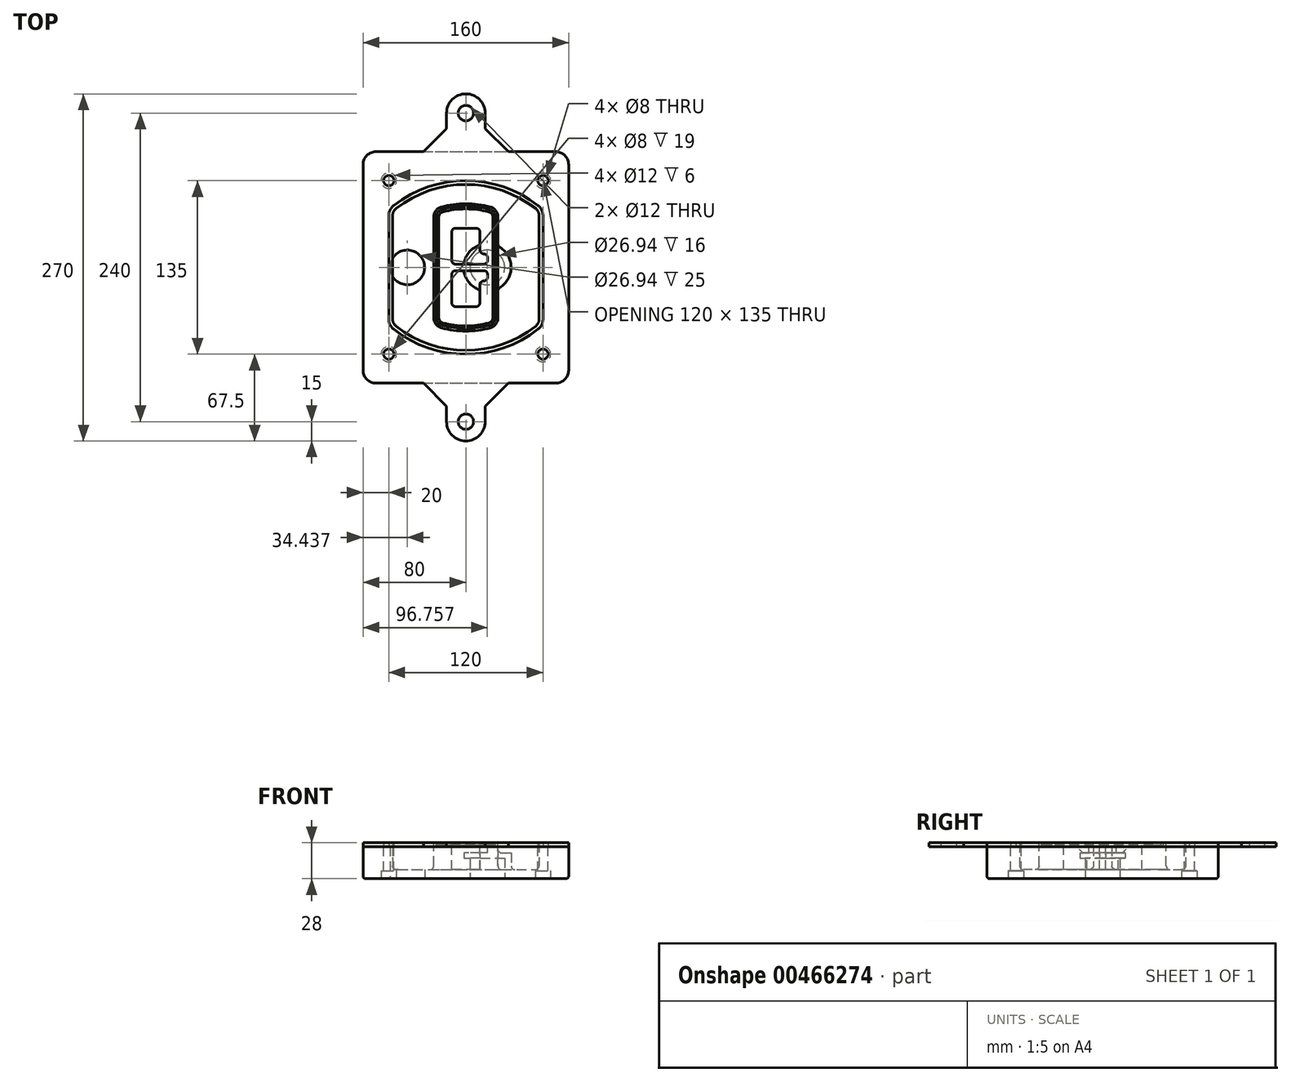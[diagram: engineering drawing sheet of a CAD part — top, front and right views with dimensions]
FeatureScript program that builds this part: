
annotation { "Feature Type Name" : "Feature", "Feature Type Description" : "" }
export const myFeature = defineFeature(function(context is Context, id is Id, definition is map)
    precondition{}
    {
        {
            var Q0;
            Q0=qCreatedBy(makeId("Top.planeOp"),FACE);
            var sketch = newSketch(context, id + "F0", { "sketchPlane" : qUnion([Q0])});
            skPoint(sketch, "E0.rect.middle", {"position": v(0, 0) * mm});
            skLineSegment(sketch, "E1.bottom", {"start": v(-70, -90) * mm, "end": v(70, -90) * mm});
            skLineSegment(sketch, "E1.top", {"start": v(-70, 90) * mm, "end": v(70, 90) * mm});
            skLineSegment(sketch, "E1.left", {"start": v(-80, -80) * mm, "end": v(-80, 80) * mm});
            skLineSegment(sketch, "E1.right", {"start": v(80, -80) * mm, "end": v(80, 80) * mm});
            skLineSegment(sketch, "E2", {"start": v(-80, 90) * mm, "end": v(80, -90) * mm, "construction": true});
            skLineSegment(sketch, "E3", {"start": v(80, 90) * mm, "end": v(-80, -90) * mm, "construction": true});
            skCircle(sketch, "E4", {"center": v(-60, 67.5) * mm, "radius": 4 * mm});
            skCircle(sketch, "E5", {"center": v(60, 67.5) * mm, "radius": 4 * mm});
            skCircle(sketch, "E6", {"center": v(60, -67.5) * mm, "radius": 4 * mm});
            skCircle(sketch, "E7", {"center": v(-60, -67.5) * mm, "radius": 4 * mm});
            skLineSegment(sketch, "E8", {"start": v(-60, 67.5) * mm, "end": v(60, 67.5) * mm, "construction": true});
            skLineSegment(sketch, "E9", {"start": v(60, 67.5) * mm, "end": v(60, -67.5) * mm, "construction": true});
            skLineSegment(sketch, "E10", {"start": v(60, -67.5) * mm, "end": v(-60, -67.5) * mm, "construction": true});
            skLineSegment(sketch, "E11", {"start": v(-60, -67.5) * mm, "end": v(-60, 67.5) * mm, "construction": true});
            skLineSegment(sketch, "E12", {"start": v(-60, 40.3) * mm, "end": v(-60, -40.3) * mm});
            skLineSegment(sketch, "E13", {"start": v(60, 40.3) * mm, "end": v(60, -40.3) * mm});
            skArc(sketch, "E14", {"start": v(56.15, 48.18) * mm, "mid": v(0, 67.5) * mm, "end": v(-56.15, 48.18) * mm});
            skArc(sketch, "E15", {"start": v(-56.15, -48.18) * mm, "mid": v(0, -67.5) * mm, "end": v(56.15, -48.18) * mm});
            skLineSegment(sketch, "E16", {"start": v(-60, 0) * mm, "end": v(60, 0) * mm, "construction": true});
            skPoint(sketch, "E17.visualSharp", {"position": v(-60, -45) * mm});
            skArc(sketch, "E17.filletArc", {"start": v(-60, -40.3) * mm, "mid": v(-58.99, -44.68) * mm, "end": v(-56.15, -48.18) * mm});
            skPoint(sketch, "E18.visualSharp", {"position": v(-60, 45) * mm});
            skArc(sketch, "E18.filletArc", {"start": v(-56.15, 48.18) * mm, "mid": v(-58.99, 44.68) * mm, "end": v(-60, 40.3) * mm});
            skPoint(sketch, "E19.visualSharp", {"position": v(60, 45) * mm});
            skArc(sketch, "E19.filletArc", {"start": v(60, 40.3) * mm, "mid": v(58.99, 44.68) * mm, "end": v(56.15, 48.18) * mm});
            skPoint(sketch, "E20.visualSharp", {"position": v(60, -45) * mm});
            skArc(sketch, "E20.filletArc", {"start": v(56.15, -48.18) * mm, "mid": v(58.99, -44.68) * mm, "end": v(60, -40.3) * mm});
            skPoint(sketch, "E21.visualSharp", {"position": v(-80, 90) * mm});
            skArc(sketch, "E21.filletArc", {"start": v(-70, 90) * mm, "mid": v(-77.07, 87.07) * mm, "end": v(-80, 80) * mm});
            skPoint(sketch, "E22.visualSharp", {"position": v(80, 90) * mm});
            skArc(sketch, "E22.filletArc", {"start": v(80, 80) * mm, "mid": v(77.07, 87.07) * mm, "end": v(70, 90) * mm});
            skPoint(sketch, "E23.visualSharp", {"position": v(80, -90) * mm});
            skArc(sketch, "E23.filletArc", {"start": v(70, -90) * mm, "mid": v(77.07, -87.07) * mm, "end": v(80, -80) * mm});
            skPoint(sketch, "E24.visualSharp", {"position": v(-80, -90) * mm});
            skArc(sketch, "E24.filletArc", {"start": v(-80, -80) * mm, "mid": v(-77.07, -87.07) * mm, "end": v(-70, -90) * mm});
            skArc(sketch, "E25.0", {"start": v(57, 40.3) * mm, "mid": v(56.3, 43.36) * mm, "end": v(54.3, 45.81) * mm});
            skLineSegment(sketch, "E25.1", {"start": v(57, 40.3) * mm, "end": v(57, -40.3) * mm});
            skArc(sketch, "E25.2", {"start": v(54.3, -45.81) * mm, "mid": v(56.3, -43.36) * mm, "end": v(57, -40.3) * mm});
            skArc(sketch, "E25.3", {"start": v(-54.3, -45.81) * mm, "mid": v(0, -64.5) * mm, "end": v(54.3, -45.81) * mm});
            skArc(sketch, "E25.4", {"start": v(-57, -40.3) * mm, "mid": v(-56.3, -43.36) * mm, "end": v(-54.3, -45.81) * mm});
            skArc(sketch, "E25.5", {"start": v(54.3, 45.81) * mm, "mid": v(0, 64.5) * mm, "end": v(-54.3, 45.81) * mm});
            skLineSegment(sketch, "E25.6", {"start": v(-57, 40.3) * mm, "end": v(-57, -40.3) * mm});
            skArc(sketch, "E25.7", {"start": v(-54.3, 45.81) * mm, "mid": v(-56.3, 43.36) * mm, "end": v(-57, 40.3) * mm});
            skArc(sketch, "E26.0", {"start": v(-58.62, 51.33) * mm, "mid": v(-62.58, 46.43) * mm, "end": v(-64, 40.3) * mm});
            skArc(sketch, "E26.1", {"start": v(58.62, 51.33) * mm, "mid": v(0, 71.5) * mm, "end": v(-58.62, 51.33) * mm});
            skArc(sketch, "E26.2", {"start": v(64, 40.3) * mm, "mid": v(62.58, 46.43) * mm, "end": v(58.62, 51.33) * mm});
            skLineSegment(sketch, "E26.3", {"start": v(64, 40.3) * mm, "end": v(64, -40.3) * mm});
            skArc(sketch, "E26.4", {"start": v(58.62, -51.33) * mm, "mid": v(62.58, -46.43) * mm, "end": v(64, -40.3) * mm});
            skLineSegment(sketch, "E26.5", {"start": v(-64, 40.3) * mm, "end": v(-64, -40.3) * mm});
            skArc(sketch, "E26.6", {"start": v(-58.62, -51.33) * mm, "mid": v(0, -71.5) * mm, "end": v(58.62, -51.33) * mm});
            skArc(sketch, "E26.7", {"start": v(-64, -40.3) * mm, "mid": v(-62.58, -46.43) * mm, "end": v(-58.62, -51.33) * mm});
            skSolve(sketch);
        }
        {
            var Q0;
            Q0=makeQuery(id+"F0.imprint","IMPRINT",FACE,{"disambiguationData":[TD([[makeQuery(id+"F0.imprint","IMPRINT",EDGE,{"derivedFrom":sQuery(id+"F0.wireOp",EDGE,"E1.bottom")}),1.0]])]});
            var Q1;
            Q1=makeQuery(id+"F0.imprint","IMPRINT",FACE,{"disambiguationData":[TD([[makeQuery(id+"F0.imprint","IMPRINT",EDGE,{"derivedFrom":sQuery(id+"F0.wireOp",EDGE,"E12")}),1.0]])]});
            var Q2;
            Q2=makeQuery(id+"F0.imprint","IMPRINT",FACE,{"disambiguationData":[TD([[makeQuery(id+"F0.imprint","IMPRINT",EDGE,{"derivedFrom":sQuery(id+"F0.wireOp",EDGE,"E25.0")}),1.0]])]});
            var Q3;
            Q3=makeQuery(id+"F0.imprint","IMPRINT",FACE,{"disambiguationData":[TD([[makeQuery(id+"F0.imprint","IMPRINT",EDGE,{"derivedFrom":sQuery(id+"F0.wireOp",EDGE,"E12")}),-1.0]])]});
            extrude(context, id + "F1", {"entities" : qUnion([Q0, Q1, Q2, Q3]), "oppositeDirection" : true, "depth" : 25 * mm});
        }
        {
            var Q0;
            Q0=makeQuery(id+"F0.imprint","IMPRINT",FACE,{"disambiguationData":[TD([[makeQuery(id+"F0.imprint","IMPRINT",EDGE,{"derivedFrom":sQuery(id+"F0.wireOp",EDGE,"E12")}),1.0]])]});
            extrude(context, id + "F2", {"entities" : qUnion([Q0]), "operationType" : NewBodyOperationType.ADD, "depth" : 3 * mm});
        }
        {
            var Q0;
            Q0=makeQuery(id+"F0.imprint","IMPRINT",FACE,{"disambiguationData":[TD([[makeQuery(id+"F0.imprint","IMPRINT",EDGE,{"derivedFrom":sQuery(id+"F0.wireOp",EDGE,"E25.0")}),1.0]])]});
            extrude(context, id + "F3", {"entities" : qUnion([Q0]), "operationType" : NewBodyOperationType.REMOVE, "oppositeDirection" : true, "depth" : 18 * mm});
        }
        {
            var Q0;
            Q0=makeQuery(id+"F2.opExtrude","CAP_FACE",FACE,{"disambiguationData":[OSD([sQuery(id+"F0.wireOp",EDGE,"E12"),sQuery(id+"F0.wireOp",EDGE,"E13"),sQuery(id+"F0.wireOp",EDGE,"E14"),sQuery(id+"F0.wireOp",EDGE,"E15"),sQuery(id+"F0.wireOp",EDGE,"E17.filletArc"),sQuery(id+"F0.wireOp",EDGE,"E18.filletArc"),sQuery(id+"F0.wireOp",EDGE,"E19.filletArc"),sQuery(id+"F0.wireOp",EDGE,"E20.filletArc"),sQuery(id+"F0.wireOp",EDGE,"E25.0"),sQuery(id+"F0.wireOp",EDGE,"E25.1"),sQuery(id+"F0.wireOp",EDGE,"E25.2"),sQuery(id+"F0.wireOp",EDGE,"E25.3"),sQuery(id+"F0.wireOp",EDGE,"E25.4"),sQuery(id+"F0.wireOp",EDGE,"E25.5"),sQuery(id+"F0.wireOp",EDGE,"E25.6"),sQuery(id+"F0.wireOp",EDGE,"E25.7")])],"isStart":false});
            var sketch = newSketch(context, id + "F4", { "sketchPlane" : qUnion([Q0])});
            skArc(sketch, "E27.0", {"start": v(-19.08, -46.97) * mm, "mid": v(0, -49.5) * mm, "end": v(19.08, -46.97) * mm});
            skArc(sketch, "E28.0", {"start": v(19.08, 46.97) * mm, "mid": v(0, 49.5) * mm, "end": v(-19.08, 46.97) * mm});
            skLineSegment(sketch, "E29", {"start": v(-25, 39.25) * mm, "end": v(-25, -39.25) * mm});
            skLineSegment(sketch, "E30", {"start": v(25, 39.25) * mm, "end": v(25, -39.25) * mm});
            skLineSegment(sketch, "E31", {"start": v(-25, 45.1) * mm, "end": v(25, 45.1) * mm, "construction": true});
            skLineSegment(sketch, "E32", {"start": v(-25, -45.1) * mm, "end": v(25, -45.1) * mm, "construction": true});
            skPoint(sketch, "E33.visualSharp", {"position": v(-25, 45.1) * mm});
            skArc(sketch, "E33.filletArc", {"start": v(-19.08, 46.97) * mm, "mid": v(-23.35, 44.11) * mm, "end": v(-25, 39.25) * mm});
            skPoint(sketch, "E34.visualSharp", {"position": v(25, 45.1) * mm});
            skArc(sketch, "E34.filletArc", {"start": v(25, 39.25) * mm, "mid": v(23.35, 44.11) * mm, "end": v(19.08, 46.97) * mm});
            skPoint(sketch, "E35.visualSharp", {"position": v(25, -45.1) * mm});
            skArc(sketch, "E35.filletArc", {"start": v(19.08, -46.97) * mm, "mid": v(23.35, -44.11) * mm, "end": v(25, -39.25) * mm});
            skPoint(sketch, "E36.visualSharp", {"position": v(-25, -45.1) * mm});
            skArc(sketch, "E36.filletArc", {"start": v(-25, -39.25) * mm, "mid": v(-23.35, -44.11) * mm, "end": v(-19.08, -46.97) * mm});
            skArc(sketch, "E37.0", {"start": v(54.3, 45.81) * mm, "mid": v(0, 64.5) * mm, "end": v(-54.3, 45.81) * mm});
            skArc(sketch, "E37.1", {"start": v(-54.3, 45.81) * mm, "mid": v(-56.3, 43.36) * mm, "end": v(-57, 40.3) * mm});
            skLineSegment(sketch, "E37.2", {"start": v(-57, 40.3) * mm, "end": v(-57, -40.3) * mm});
            skArc(sketch, "E37.3", {"start": v(-57, -40.3) * mm, "mid": v(-56.3, -43.36) * mm, "end": v(-54.3, -45.81) * mm});
            skArc(sketch, "E37.4", {"start": v(-54.3, -45.81) * mm, "mid": v(0, -64.5) * mm, "end": v(54.3, -45.81) * mm});
            skArc(sketch, "E37.5", {"start": v(54.3, -45.81) * mm, "mid": v(56.3, -43.36) * mm, "end": v(57, -40.3) * mm});
            skLineSegment(sketch, "E37.6", {"start": v(57, 40.3) * mm, "end": v(57, -40.3) * mm});
            skArc(sketch, "E37.7", {"start": v(57, 40.3) * mm, "mid": v(56.3, 43.36) * mm, "end": v(54.3, 45.81) * mm});
            skLineSegment(sketch, "E38.0", {"start": v(23, 39.25) * mm, "end": v(23, -39.25) * mm});
            skArc(sketch, "E38.1", {"start": v(18.56, -45.04) * mm, "mid": v(21.76, -42.9) * mm, "end": v(23, -39.25) * mm});
            skArc(sketch, "E38.2", {"start": v(-18.56, -45.04) * mm, "mid": v(0, -47.5) * mm, "end": v(18.56, -45.04) * mm});
            skArc(sketch, "E38.3", {"start": v(-23, -39.25) * mm, "mid": v(-21.76, -42.9) * mm, "end": v(-18.56, -45.04) * mm});
            skLineSegment(sketch, "E38.4", {"start": v(-23, 39.25) * mm, "end": v(-23, -39.25) * mm});
            skArc(sketch, "E38.5", {"start": v(23, 39.25) * mm, "mid": v(21.76, 42.9) * mm, "end": v(18.56, 45.04) * mm});
            skArc(sketch, "E38.6", {"start": v(-18.56, 45.04) * mm, "mid": v(-21.76, 42.9) * mm, "end": v(-23, 39.25) * mm});
            skArc(sketch, "E38.7", {"start": v(18.56, 45.04) * mm, "mid": v(0, 47.5) * mm, "end": v(-18.56, 45.04) * mm});
            skArc(sketch, "E39.0", {"start": v(21, 39.25) * mm, "mid": v(20.18, 41.68) * mm, "end": v(18.04, 43.1) * mm});
            skLineSegment(sketch, "E39.1", {"start": v(21, 39.25) * mm, "end": v(21, -39.25) * mm});
            skArc(sketch, "E39.2", {"start": v(18.04, -43.1) * mm, "mid": v(20.18, -41.68) * mm, "end": v(21, -39.25) * mm});
            skArc(sketch, "E39.3", {"start": v(-18.04, -43.1) * mm, "mid": v(0, -45.5) * mm, "end": v(18.04, -43.1) * mm});
            skArc(sketch, "E39.4", {"start": v(-21, -39.25) * mm, "mid": v(-20.18, -41.68) * mm, "end": v(-18.04, -43.1) * mm});
            skArc(sketch, "E39.5", {"start": v(18.04, 43.1) * mm, "mid": v(0, 45.5) * mm, "end": v(-18.04, 43.1) * mm});
            skLineSegment(sketch, "E39.6", {"start": v(-21, 39.25) * mm, "end": v(-21, -39.25) * mm});
            skArc(sketch, "E39.7", {"start": v(-18.04, 43.1) * mm, "mid": v(-20.18, 41.68) * mm, "end": v(-21, 39.25) * mm});
            skLineSegment(sketch, "E40", {"start": v(-25, 0) * mm, "end": v(25, 0) * mm, "construction": true});
            skLineSegment(sketch, "E41", {"start": v(-11, 5.5) * mm, "end": v(-11, 27.5) * mm});
            skLineSegment(sketch, "E42", {"start": v(-8, 30.5) * mm, "end": v(8, 30.5) * mm});
            skLineSegment(sketch, "E43", {"start": v(11, 27.5) * mm, "end": v(11, 13.5) * mm});
            skLineSegment(sketch, "E44", {"start": v(14, 10.5) * mm, "end": v(14, 10.5) * mm});
            skLineSegment(sketch, "E45", {"start": v(17, 7.5) * mm, "end": v(17, 5.5) * mm});
            skLineSegment(sketch, "E46", {"start": v(14, 2.5) * mm, "end": v(-8, 2.5) * mm});
            skPoint(sketch, "E47.visualSharp", {"position": v(-11, 30.5) * mm});
            skArc(sketch, "E47.filletArc", {"start": v(-8, 30.5) * mm, "mid": v(-10.12, 29.62) * mm, "end": v(-11, 27.5) * mm});
            skPoint(sketch, "E48.visualSharp", {"position": v(11, 30.5) * mm});
            skArc(sketch, "E48.filletArc", {"start": v(11, 27.5) * mm, "mid": v(10.12, 29.62) * mm, "end": v(8, 30.5) * mm});
            skPoint(sketch, "E49.visualSharp", {"position": v(11, 10.5) * mm});
            skArc(sketch, "E49.filletArc", {"start": v(11, 13.5) * mm, "mid": v(11.88, 11.38) * mm, "end": v(14, 10.5) * mm});
            skPoint(sketch, "E50.visualSharp", {"position": v(17, 10.5) * mm});
            skArc(sketch, "E50.filletArc", {"start": v(17, 7.5) * mm, "mid": v(16.12, 9.62) * mm, "end": v(14, 10.5) * mm});
            skPoint(sketch, "E51.visualSharp", {"position": v(17, 2.5) * mm});
            skArc(sketch, "E51.filletArc", {"start": v(14, 2.5) * mm, "mid": v(16.12, 3.38) * mm, "end": v(17, 5.5) * mm});
            skPoint(sketch, "E52.visualSharp", {"position": v(-11, 2.5) * mm});
            skArc(sketch, "E52.filletArc", {"start": v(-11, 5.5) * mm, "mid": v(-10.12, 3.38) * mm, "end": v(-8, 2.5) * mm});
            skLineSegment(sketch, "E53.0.MirrorCS", {"start": v(14, -2.5) * mm, "end": v(-8, -2.5) * mm});
            skArc(sketch, "E54.0.MirrorCS", {"start": v(-11, -5.5) * mm, "mid": v(-10.12, -3.38) * mm, "end": v(-8, -2.5) * mm});
            skLineSegment(sketch, "E55.0.MirrorCS", {"start": v(-11, -5.5) * mm, "end": v(-11, -27.5) * mm});
            skArc(sketch, "E56.0.MirrorCS", {"start": v(-8, -30.5) * mm, "mid": v(-10.12, -29.62) * mm, "end": v(-11, -27.5) * mm});
            skLineSegment(sketch, "E57.0.MirrorCS", {"start": v(-8, -30.5) * mm, "end": v(8, -30.5) * mm});
            skArc(sketch, "E58.0.MirrorCS", {"start": v(11, -27.5) * mm, "mid": v(10.12, -29.62) * mm, "end": v(8, -30.5) * mm});
            skLineSegment(sketch, "E59.0.MirrorCS", {"start": v(11, -27.5) * mm, "end": v(11, -13.5) * mm});
            skArc(sketch, "E60.0.MirrorCS", {"start": v(11, -13.5) * mm, "mid": v(11.88, -11.38) * mm, "end": v(14, -10.5) * mm});
            skArc(sketch, "E61.0.MirrorCS", {"start": v(17, -7.5) * mm, "mid": v(16.12, -9.62) * mm, "end": v(14, -10.5) * mm});
            skLineSegment(sketch, "E62.0.MirrorCS", {"start": v(17, -7.5) * mm, "end": v(17, -5.5) * mm});
            skArc(sketch, "E63.0.MirrorCS", {"start": v(14, -2.5) * mm, "mid": v(16.12, -3.38) * mm, "end": v(17, -5.5) * mm});
            skSolve(sketch);
        }
        {
            var Q0;
            Q0=makeQuery(id+"F4.imprint","IMPRINT",FACE,{"disambiguationData":[TD([[makeQuery(id+"F4.imprint","IMPRINT",EDGE,{"derivedFrom":sQuery(id+"F4.wireOp",EDGE,"E27.0")}),1.0]])]});
            var Q1;
            Q1=makeQuery(id+"F4.imprint","IMPRINT",FACE,{"disambiguationData":[TD([[makeQuery(id+"F4.imprint","IMPRINT",EDGE,{"derivedFrom":sQuery(id+"F4.wireOp",EDGE,"E38.0")}),-1.0]])]});
            var Q2;
            Q2=makeQuery(id+"F4.imprint","IMPRINT",FACE,{"disambiguationData":[TD([[makeQuery(id+"F4.imprint","IMPRINT",EDGE,{"derivedFrom":sQuery(id+"F4.wireOp",EDGE,"E39.0")}),1.0]])]});
            extrude(context, id + "F5", {"entities" : qUnion([Q0, Q1, Q2]), "operationType" : NewBodyOperationType.ADD, "endBound" : BoundingType.UP_TO_NEXT, "oppositeDirection" : true, "depth" : 25 * mm});
        }
        {
            var Q0;
            Q0=makeQuery(id+"F4.imprint","IMPRINT",FACE,{"disambiguationData":[TD([[makeQuery(id+"F4.imprint","IMPRINT",EDGE,{"derivedFrom":sQuery(id+"F4.wireOp",EDGE,"E38.0")}),-1.0]])]});
            extrude(context, id + "F6", {"entities" : qUnion([Q0]), "operationType" : NewBodyOperationType.REMOVE, "oppositeDirection" : true, "depth" : 2 * mm});
        }
        {
            var Q0;
            Q0=makeQuery(id+"F1.opExtrude","CAP_FACE",FACE,{"disambiguationData":[OSD([sQuery(id+"F0.wireOp",EDGE,"E1.bottom"),sQuery(id+"F0.wireOp",EDGE,"E1.top"),sQuery(id+"F0.wireOp",EDGE,"E1.left"),sQuery(id+"F0.wireOp",EDGE,"E1.right"),sQuery(id+"F0.wireOp",EDGE,"E4"),sQuery(id+"F0.wireOp",EDGE,"E5"),sQuery(id+"F0.wireOp",EDGE,"E6"),sQuery(id+"F0.wireOp",EDGE,"E7"),sQuery(id+"F0.wireOp",EDGE,"E21.filletArc"),sQuery(id+"F0.wireOp",EDGE,"E22.filletArc"),sQuery(id+"F0.wireOp",EDGE,"E23.filletArc"),sQuery(id+"F0.wireOp",EDGE,"E24.filletArc")])],"isStart":false});
            var sketch = newSketch(context, id + "F7", { "sketchPlane" : qUnion([Q0])});
            skCircle(sketch, "E64", {"center": v(16.76, 0) * mm, "radius": 13.47 * mm});
            skCircle(sketch, "E65", {"center": v(-45.56, 0) * mm, "radius": 13.47 * mm});
            skLineSegment(sketch, "E66", {"start": v(80, 0) * mm, "end": v(-80, 0) * mm});
            skCircle(sketch, "E67", {"center": v(16.76, 0) * mm, "radius": 18.47 * mm});
            skCircle(sketch, "E68", {"center": v(60, -67.5) * mm, "radius": 6 * mm});
            skCircle(sketch, "E69", {"center": v(-60, -67.5) * mm, "radius": 6 * mm});
            skCircle(sketch, "E70", {"center": v(-60, 67.5) * mm, "radius": 6 * mm});
            skCircle(sketch, "E71", {"center": v(60, 67.5) * mm, "radius": 6 * mm});
            skSolve(sketch);
        }
        {
            var Q0;
            {var subQ1=sQuery(id+"F7.wireOp",EDGE,"E66");var subQ4=sQuery(id+"F7.wireOp",EDGE,"E64");var subQ6=makeQuery(id+"F7.imprint","INTERSECT",VERTEX,{"disambiguationData":[OD(0.0)],"derivedFrom":[subQ4,subQ1]});Q0=makeQuery(id+"F7.imprint","IMPRINT",FACE,{"disambiguationData":[TD([[makeQuery(id+"F7.imprint","IMPRINT",EDGE,{"disambiguationData":[TD([[subQ6,-1.0]])],"derivedFrom":subQ4}),-1.0]])]});}
            var Q1;
            {var subQ0=sQuery(id+"F7.wireOp",EDGE,"E66");var subQ1=sQuery(id+"F7.wireOp",EDGE,"E64");var subQ3=makeQuery(id+"F7.imprint","INTERSECT",VERTEX,{"disambiguationData":[OD(0.0)],"derivedFrom":[subQ1,subQ0]});Q1=makeQuery(id+"F7.imprint","IMPRINT",FACE,{"disambiguationData":[TD([[makeQuery(id+"F7.imprint","IMPRINT",EDGE,{"disambiguationData":[TD([[subQ3,-1.0]])],"derivedFrom":subQ1}),1.0]])]});}
            var Q2;
            {var subQ0=sQuery(id+"F7.wireOp",EDGE,"E66");var subQ1=sQuery(id+"F7.wireOp",EDGE,"E64");var subQ3=makeQuery(id+"F7.imprint","INTERSECT",VERTEX,{"disambiguationData":[OD(0.0)],"derivedFrom":[subQ1,subQ0]});Q2=makeQuery(id+"F7.imprint","IMPRINT",FACE,{"disambiguationData":[TD([[makeQuery(id+"F7.imprint","IMPRINT",EDGE,{"disambiguationData":[TD([[subQ3,1.0]])],"derivedFrom":subQ1}),1.0]])]});}
            var Q3;
            {var subQ1=sQuery(id+"F7.wireOp",EDGE,"E66");var subQ4=sQuery(id+"F7.wireOp",EDGE,"E64");var subQ6=makeQuery(id+"F7.imprint","INTERSECT",VERTEX,{"disambiguationData":[OD(0.0)],"derivedFrom":[subQ4,subQ1]});Q3=makeQuery(id+"F7.imprint","IMPRINT",FACE,{"disambiguationData":[TD([[makeQuery(id+"F7.imprint","IMPRINT",EDGE,{"disambiguationData":[TD([[subQ6,1.0]])],"derivedFrom":subQ4}),-1.0]])]});}
            extrude(context, id + "F8", {"entities" : qUnion([Q0, Q1, Q2, Q3]), "operationType" : NewBodyOperationType.ADD, "oppositeDirection" : true, "depth" : 20 * mm});
        }
        {
            var Q0;
            {var subQ0=sQuery(id+"F7.wireOp",EDGE,"E66");var subQ1=sQuery(id+"F7.wireOp",EDGE,"E64");var subQ3=makeQuery(id+"F7.imprint","INTERSECT",VERTEX,{"disambiguationData":[OD(0.0)],"derivedFrom":[subQ1,subQ0]});Q0=makeQuery(id+"F7.imprint","IMPRINT",FACE,{"disambiguationData":[TD([[makeQuery(id+"F7.imprint","IMPRINT",EDGE,{"disambiguationData":[TD([[subQ3,-1.0]])],"derivedFrom":subQ1}),1.0]])]});}
            var Q1;
            {var subQ0=sQuery(id+"F7.wireOp",EDGE,"E66");var subQ1=sQuery(id+"F7.wireOp",EDGE,"E64");var subQ3=makeQuery(id+"F7.imprint","INTERSECT",VERTEX,{"disambiguationData":[OD(0.0)],"derivedFrom":[subQ1,subQ0]});Q1=makeQuery(id+"F7.imprint","IMPRINT",FACE,{"disambiguationData":[TD([[makeQuery(id+"F7.imprint","IMPRINT",EDGE,{"disambiguationData":[TD([[subQ3,1.0]])],"derivedFrom":subQ1}),1.0]])]});}
            extrude(context, id + "F9", {"entities" : qUnion([Q0, Q1]), "operationType" : NewBodyOperationType.REMOVE, "oppositeDirection" : true, "depth" : 16 * mm});
        }
        {
            var Q0;
            {var subQ0=sQuery(id+"F7.wireOp",EDGE,"E66");var subQ1=sQuery(id+"F7.wireOp",EDGE,"E65");var subQ3=makeQuery(id+"F7.imprint","INTERSECT",VERTEX,{"disambiguationData":[OD(0.0)],"derivedFrom":[subQ1,subQ0]});Q0=makeQuery(id+"F7.imprint","IMPRINT",FACE,{"disambiguationData":[TD([[makeQuery(id+"F7.imprint","IMPRINT",EDGE,{"disambiguationData":[TD([[subQ3,-1.0]])],"derivedFrom":subQ1}),1.0]])]});}
            var Q1;
            {var subQ0=sQuery(id+"F7.wireOp",EDGE,"E66");var subQ1=sQuery(id+"F7.wireOp",EDGE,"E65");var subQ3=makeQuery(id+"F7.imprint","INTERSECT",VERTEX,{"disambiguationData":[OD(0.0)],"derivedFrom":[subQ1,subQ0]});Q1=makeQuery(id+"F7.imprint","IMPRINT",FACE,{"disambiguationData":[TD([[makeQuery(id+"F7.imprint","IMPRINT",EDGE,{"disambiguationData":[TD([[subQ3,1.0]])],"derivedFrom":subQ1}),1.0]])]});}
            extrude(context, id + "F10", {"entities" : qUnion([Q0, Q1]), "operationType" : NewBodyOperationType.REMOVE, "oppositeDirection" : true, "depth" : 25 * mm});
        }
        {
            var Q0;
            Q0=makeQuery(id+"F7.imprint","IMPRINT",FACE,{"disambiguationData":[TD([[makeQuery(id+"F7.imprint","IMPRINT",EDGE,{"derivedFrom":sQuery(id+"F7.wireOp",EDGE,"E68")}),1.0]])]});
            var Q1;
            Q1=makeQuery(id+"F7.imprint","IMPRINT",FACE,{"disambiguationData":[TD([[makeQuery(id+"F7.imprint","IMPRINT",EDGE,{"derivedFrom":makeQuery(id+"F1.opExtrude","CAP_EDGE",EDGE,{"disambiguationData":[OSD([sQuery(id+"F0.wireOp",EDGE,"E5")])],"isStart":false})}),-1.0]])]});
            var Q2;
            Q2=makeQuery(id+"F7.imprint","IMPRINT",FACE,{"disambiguationData":[TD([[makeQuery(id+"F7.imprint","IMPRINT",EDGE,{"derivedFrom":sQuery(id+"F7.wireOp",EDGE,"E69")}),1.0]])]});
            var Q3;
            Q3=makeQuery(id+"F7.imprint","IMPRINT",FACE,{"disambiguationData":[TD([[makeQuery(id+"F7.imprint","IMPRINT",EDGE,{"derivedFrom":makeQuery(id+"F1.opExtrude","CAP_EDGE",EDGE,{"disambiguationData":[OSD([sQuery(id+"F0.wireOp",EDGE,"E4")])],"isStart":false})}),-1.0]])]});
            var Q4;
            Q4=makeQuery(id+"F7.imprint","IMPRINT",FACE,{"disambiguationData":[TD([[makeQuery(id+"F7.imprint","IMPRINT",EDGE,{"derivedFrom":sQuery(id+"F7.wireOp",EDGE,"E70")}),1.0]])]});
            var Q5;
            Q5=makeQuery(id+"F7.imprint","IMPRINT",FACE,{"disambiguationData":[TD([[makeQuery(id+"F7.imprint","IMPRINT",EDGE,{"derivedFrom":makeQuery(id+"F1.opExtrude","CAP_EDGE",EDGE,{"disambiguationData":[OSD([sQuery(id+"F0.wireOp",EDGE,"E7")])],"isStart":false})}),-1.0]])]});
            var Q6;
            Q6=makeQuery(id+"F7.imprint","IMPRINT",FACE,{"disambiguationData":[TD([[makeQuery(id+"F7.imprint","IMPRINT",EDGE,{"derivedFrom":sQuery(id+"F7.wireOp",EDGE,"E71")}),1.0]])]});
            var Q7;
            Q7=makeQuery(id+"F7.imprint","IMPRINT",FACE,{"disambiguationData":[TD([[makeQuery(id+"F7.imprint","IMPRINT",EDGE,{"derivedFrom":makeQuery(id+"F1.opExtrude","CAP_EDGE",EDGE,{"disambiguationData":[OSD([sQuery(id+"F0.wireOp",EDGE,"E6")])],"isStart":false})}),-1.0]])]});
            extrude(context, id + "F11", {"entities" : qUnion([Q0, Q1, Q2, Q3, Q4, Q5, Q6, Q7]), "operationType" : NewBodyOperationType.REMOVE, "oppositeDirection" : true, "depth" : 6 * mm});
        }
        {
            var Q0;
            Q0=makeQuery(id+"F9.boolean.opBoolean","COPY",FACE,{"derivedFrom":makeQuery(id+"F9.opExtrude","CAP_FACE",FACE,{"disambiguationData":[OSD([sQuery(id+"F7.wireOp",EDGE,"E64")])],"isStart":false})});
            var sketch = newSketch(context, id + "F12", { "sketchPlane" : qUnion([Q0])});
            skArc(sketch, "E72.0", {"start": v(11, 17.55) * mm, "mid": v(2.57, 11.82) * mm, "end": v(-1.54, 2.5) * mm});
            skArc(sketch, "E72.1", {"start": v(-1.54, -2.5) * mm, "mid": v(2.57, -11.82) * mm, "end": v(11, -17.55) * mm});
            skLineSegment(sketch, "E73", {"start": v(-1.54, -2.5) * mm, "end": v(14, -2.5) * mm});
            skLineSegment(sketch, "E74.0", {"start": v(14, 2.5) * mm, "end": v(-1.54, 2.5) * mm});
            skArc(sketch, "E74.1", {"start": v(14, 2.5) * mm, "mid": v(16.12, 3.38) * mm, "end": v(17, 5.5) * mm});
            skLineSegment(sketch, "E74.2", {"start": v(17, 7.5) * mm, "end": v(17, 5.5) * mm});
            skArc(sketch, "E74.3", {"start": v(17, 7.5) * mm, "mid": v(16.12, 9.62) * mm, "end": v(14, 10.5) * mm});
            skArc(sketch, "E74.4", {"start": v(11, 13.5) * mm, "mid": v(11.88, 11.38) * mm, "end": v(14, 10.5) * mm});
            skLineSegment(sketch, "E74.5", {"start": v(11, 17.55) * mm, "end": v(11, 13.5) * mm});
            skLineSegment(sketch, "E74.7", {"start": v(14, -2.5) * mm, "end": v(-1.54, -2.5) * mm});
            skArc(sketch, "E74.8", {"start": v(14, -2.5) * mm, "mid": v(16.12, -3.38) * mm, "end": v(17, -5.5) * mm});
            skLineSegment(sketch, "E74.9", {"start": v(17, -7.5) * mm, "end": v(17, -5.5) * mm});
            skArc(sketch, "E74.10", {"start": v(17, -7.5) * mm, "mid": v(16.12, -9.62) * mm, "end": v(14, -10.5) * mm});
            skArc(sketch, "E74.11", {"start": v(11, -13.5) * mm, "mid": v(11.88, -11.38) * mm, "end": v(14, -10.5) * mm});
            skLineSegment(sketch, "E74.12", {"start": v(11, -17.55) * mm, "end": v(11, -13.5) * mm});
            skPoint(sketch, "E75.orphan", {"position": v(11, -27.5) * mm});
            skPoint(sketch, "E76.orphan", {"position": v(-8, -2.5) * mm});
            skPoint(sketch, "E77.orphan", {"position": v(-8, 2.5) * mm});
            skPoint(sketch, "E78.orphan", {"position": v(11, 27.5) * mm});
            skSolve(sketch);
        }
        {
            var Q0;
            {var subQ7=sQuery(id+"F12.wireOp",EDGE,"E72.0");var subQ14=sQuery(id+"F12.wireOp",EDGE,"E72.1");var subQ16=sQuery(id+"F12.wireOp",EDGE,"E74.1");var subQ18=sQuery(id+"F12.wireOp",EDGE,"E74.8");Q0=qUnion([makeQuery(id+"F12.imprint","IMPRINT",FACE,{"disambiguationData":[TD([[makeQuery(id+"F12.imprint","IMPRINT",EDGE,{"derivedFrom":subQ7}),1.0]])]}),makeQuery(id+"F12.imprint","IMPRINT",FACE,{"disambiguationData":[TD([[makeQuery(id+"F12.imprint","IMPRINT",EDGE,{"derivedFrom":subQ14}),1.0]])]}),makeQuery(id+"F12.imprint","IMPRINT",FACE,{"disambiguationData":[TD([[makeQuery(id+"F12.imprint","IMPRINT",EDGE,{"derivedFrom":subQ16}),1.0]])]}),makeQuery(id+"F12.imprint","IMPRINT",FACE,{"disambiguationData":[TD([[makeQuery(id+"F12.imprint","IMPRINT",EDGE,{"derivedFrom":subQ18}),-1.0]])]})]);}
            var Q1;
            Q1=makeQuery(id+"F5.boolean.opBoolean","SPLIT",FACE,{"disambiguationData":[TD([makeQuery(id+"F5.opExtrude","SWEPT_FACE",FACE,{"disambiguationData":[OSD([sQuery(id+"F4.wireOp",EDGE,"E41")])]})])],"derivedFrom":makeQuery(id+"F3.boolean.opBoolean","COPY",FACE,{"derivedFrom":makeQuery(id+"F3.opExtrude","CAP_FACE",FACE,{"disambiguationData":[OSD([sQuery(id+"F0.wireOp",EDGE,"E25.0"),sQuery(id+"F0.wireOp",EDGE,"E25.1"),sQuery(id+"F0.wireOp",EDGE,"E25.2"),sQuery(id+"F0.wireOp",EDGE,"E25.3"),sQuery(id+"F0.wireOp",EDGE,"E25.4"),sQuery(id+"F0.wireOp",EDGE,"E25.5"),sQuery(id+"F0.wireOp",EDGE,"E25.6"),sQuery(id+"F0.wireOp",EDGE,"E25.7")])],"isStart":false})})});
            extrude(context, id + "F13", {"entities" : qUnion([Q0]), "operationType" : NewBodyOperationType.REMOVE, "endBound" : BoundingType.UP_TO_SURFACE, "endBoundEntityFace" : qUnion([Q1]), "depth" : 25 * mm});
        }
        {
            var Q0;
            Q0=makeQuery(id+"F3.boolean.opBoolean","COPY",EDGE,{"derivedFrom":makeQuery(id+"F3.opExtrude","CAP_EDGE",EDGE,{"disambiguationData":[OSD([sQuery(id+"F0.wireOp",EDGE,"E25.6")])],"isStart":false})});
            var Q1;
            Q1=makeQuery(id+"F8.boolean.opBoolean","INTERSECT",EDGE,{"derivedFrom":[makeQuery(id+"F5.opExtrude","SWEPT_FACE",FACE,{"disambiguationData":[OSD([sQuery(id+"F4.wireOp",EDGE,"E30")])]}),makeQuery(id+"F8.opExtrude","CAP_FACE",FACE,{"disambiguationData":[OSD([sQuery(id+"F7.wireOp",EDGE,"E67")])],"isStart":false})]});
            var Q2;
            Q2=makeQuery(id+"F8.boolean.opBoolean","INTERSECT",EDGE,{"disambiguationData":[OD(1.0)],"derivedFrom":[makeQuery(id+"F5.opExtrude","SWEPT_FACE",FACE,{"disambiguationData":[OSD([sQuery(id+"F4.wireOp",EDGE,"E30")])]}),makeQuery(id+"F8.opExtrude","SWEPT_FACE",FACE,{"disambiguationData":[OSD([sQuery(id+"F7.wireOp",EDGE,"E67")])]})]});
            var Q3;
            {var subQ0=sQuery(id+"F4.wireOp",EDGE,"E30");Q3=makeQuery(id+"F8.boolean.opBoolean","SPLIT",EDGE,{"disambiguationData":[TD([makeQuery(id+"F5.opExtrude","SWEPT_FACE",FACE,{"disambiguationData":[OSD([sQuery(id+"F4.wireOp",EDGE,"E35.filletArc")])]})])],"derivedFrom":makeQuery(id+"F5.opExtrude","CAP_EDGE",EDGE,{"disambiguationData":[OSD([subQ0])],"isStart":false})});}
            var Q4;
            {var subQ0=sQuery(id+"F0.wireOp",EDGE,"E25.7");var subQ1=sQuery(id+"F0.wireOp",EDGE,"E25.1");var subQ2=sQuery(id+"F0.wireOp",EDGE,"E25.6");var subQ3=sQuery(id+"F0.wireOp",EDGE,"E25.5");var subQ4=sQuery(id+"F0.wireOp",EDGE,"E25.4");var subQ5=sQuery(id+"F0.wireOp",EDGE,"E25.0");var subQ6=sQuery(id+"F0.wireOp",EDGE,"E25.2");var subQ7=sQuery(id+"F0.wireOp",EDGE,"E25.3");Q4=makeQuery(id+"F8.boolean.opBoolean","INTERSECT",EDGE,{"derivedFrom":[makeQuery(id+"F5.boolean.opBoolean","SPLIT",FACE,{"disambiguationData":[TD([makeQuery(id+"F2.opExtrude","SWEPT_FACE",FACE,{"disambiguationData":[OSD([subQ5])]})])],"derivedFrom":makeQuery(id+"F3.boolean.opBoolean","COPY",FACE,{"derivedFrom":makeQuery(id+"F3.opExtrude","CAP_FACE",FACE,{"disambiguationData":[OSD([subQ5,subQ1,subQ6,subQ7,subQ4,subQ3,subQ2,subQ0])],"isStart":false})})}),makeQuery(id+"F8.opExtrude","SWEPT_FACE",FACE,{"disambiguationData":[OSD([sQuery(id+"F7.wireOp",EDGE,"E67")])]})]});}
            var Q5;
            Q5=makeQuery(id+"F8.boolean.opBoolean","INTERSECT",EDGE,{"disambiguationData":[OD(0.0)],"derivedFrom":[makeQuery(id+"F5.opExtrude","SWEPT_FACE",FACE,{"disambiguationData":[OSD([sQuery(id+"F4.wireOp",EDGE,"E30")])]}),makeQuery(id+"F8.opExtrude","SWEPT_FACE",FACE,{"disambiguationData":[OSD([sQuery(id+"F7.wireOp",EDGE,"E67")])]})]});
            fillet(context, id + "F14", {"entities" : qUnion([Q0, Q1, Q2, Q3, Q4, Q5]), "radius" : 3 * mm, "tangentPropagation" : true, "allowEdgeOverflow" : false});
        }
        {
            var Q0;
            Q0=makeQuery(id+"F1.opExtrude","CAP_EDGE",EDGE,{"disambiguationData":[OSD([sQuery(id+"F0.wireOp",EDGE,"E1.bottom")])],"isStart":false});
            fillet(context, id + "F15", {"entities" : qUnion([Q0]), "radius" : 2 * mm, "tangentPropagation" : true, "allowEdgeOverflow" : false});
        }
        {
            var Q0;
            {var subQ0=sQuery(id+"F0.wireOp",EDGE,"E21.filletArc");var subQ1=sQuery(id+"F0.wireOp",EDGE,"E7");var subQ2=sQuery(id+"F0.wireOp",EDGE,"E6");var subQ3=sQuery(id+"F0.wireOp",EDGE,"E5");var subQ4=sQuery(id+"F0.wireOp",EDGE,"E4");var subQ5=sQuery(id+"F0.wireOp",EDGE,"E22.filletArc");var subQ6=sQuery(id+"F0.wireOp",EDGE,"E1.bottom");var subQ7=sQuery(id+"F0.wireOp",EDGE,"E1.right");var subQ8=sQuery(id+"F0.wireOp",EDGE,"E1.top");var subQ9=sQuery(id+"F0.wireOp",EDGE,"E1.left");var subQ10=sQuery(id+"F0.wireOp",EDGE,"E23.filletArc");var subQ11=sQuery(id+"F0.wireOp",EDGE,"E24.filletArc");Q0=makeQuery(id+"F2.boolean.opBoolean","SPLIT",FACE,{"disambiguationData":[TD([makeQuery(id+"F1.opExtrude","SWEPT_FACE",FACE,{"disambiguationData":[OSD([subQ6])]})])],"derivedFrom":makeQuery(id+"F1.opExtrude","CAP_FACE",FACE,{"disambiguationData":[OSD([subQ6,subQ8,subQ9,subQ7,subQ4,subQ3,subQ2,subQ1,subQ0,subQ5,subQ10,subQ11])],"isStart":true})});}
            var sketch = newSketch(context, id + "F16", { "sketchPlane" : qUnion([Q0])});
            skLineSegment(sketch, "E79", {"start": v(0, 90) * mm, "end": v(0, 120) * mm, "construction": true});
            skLineSegment(sketch, "E80", {"start": v(-33, 90) * mm, "end": v(-15, 108) * mm});
            skLineSegment(sketch, "E81", {"start": v(-15, 108) * mm, "end": v(-15, 120) * mm});
            skLineSegment(sketch, "E82", {"start": v(33, 90) * mm, "end": v(15, 108) * mm});
            skLineSegment(sketch, "E83", {"start": v(15, 108) * mm, "end": v(15, 120) * mm});
            skArc(sketch, "E84", {"start": v(15, 120) * mm, "mid": v(0, 135) * mm, "end": v(-15, 120) * mm});
            skCircle(sketch, "E85", {"center": v(0, 120) * mm, "radius": 6 * mm});
            skLineSegment(sketch, "E86", {"start": v(0, -90) * mm, "end": v(0, -120) * mm, "construction": true});
            skLineSegment(sketch, "E87", {"start": v(33, -90) * mm, "end": v(15, -108) * mm});
            skLineSegment(sketch, "E88", {"start": v(15, -108) * mm, "end": v(15, -120) * mm});
            skLineSegment(sketch, "E89", {"start": v(-33, -90) * mm, "end": v(-15, -108) * mm});
            skLineSegment(sketch, "E90", {"start": v(-15, -108) * mm, "end": v(-15, -120) * mm});
            skCircle(sketch, "E91", {"center": v(0, -120) * mm, "radius": 6 * mm});
            skArc(sketch, "E92", {"start": v(-15, -120) * mm, "mid": v(0, -135) * mm, "end": v(15, -120) * mm});
            skLineSegment(sketch, "E93", {"start": v(80, 0) * mm, "end": v(-80, 0) * mm, "construction": true});
            skSolve(sketch);
        }
        {
            var Q0;
            {var subQ1=sQuery(id+"F16.wireOp",EDGE,"E87");Q0=makeQuery(id+"F16.imprint","IMPRINT",FACE,{"disambiguationData":[TD([[makeQuery(id+"F16.imprint","IMPRINT",EDGE,{"derivedFrom":subQ1}),-1.0]])]});}
            var Q1;
            Q1=makeQuery(id+"F16.imprint","IMPRINT",FACE,{"disambiguationData":[TD([[makeQuery(id+"F16.imprint","IMPRINT",EDGE,{"derivedFrom":makeQuery(id+"F1.opExtrude","CAP_EDGE",EDGE,{"disambiguationData":[OSD([sQuery(id+"F0.wireOp",EDGE,"E1.left")])],"isStart":true})}),-1.0]])]});
            var Q2;
            {var subQ1=sQuery(id+"F16.wireOp",EDGE,"E80");Q2=makeQuery(id+"F16.imprint","IMPRINT",FACE,{"disambiguationData":[TD([[makeQuery(id+"F16.imprint","IMPRINT",EDGE,{"derivedFrom":subQ1}),-1.0]])]});}
            var Q3;
            Q3=makeQuery(id+"F2.opExtrude","CAP_FACE",FACE,{"disambiguationData":[OSD([sQuery(id+"F0.wireOp",EDGE,"E12"),sQuery(id+"F0.wireOp",EDGE,"E13"),sQuery(id+"F0.wireOp",EDGE,"E14"),sQuery(id+"F0.wireOp",EDGE,"E15"),sQuery(id+"F0.wireOp",EDGE,"E17.filletArc"),sQuery(id+"F0.wireOp",EDGE,"E18.filletArc"),sQuery(id+"F0.wireOp",EDGE,"E19.filletArc"),sQuery(id+"F0.wireOp",EDGE,"E20.filletArc"),sQuery(id+"F0.wireOp",EDGE,"E25.0"),sQuery(id+"F0.wireOp",EDGE,"E25.1"),sQuery(id+"F0.wireOp",EDGE,"E25.2"),sQuery(id+"F0.wireOp",EDGE,"E25.3"),sQuery(id+"F0.wireOp",EDGE,"E25.4"),sQuery(id+"F0.wireOp",EDGE,"E25.5"),sQuery(id+"F0.wireOp",EDGE,"E25.6"),sQuery(id+"F0.wireOp",EDGE,"E25.7")])],"isStart":false});
            extrude(context, id + "F17", {"entities" : qUnion([Q0, Q1, Q2]), "endBound" : BoundingType.UP_TO_SURFACE, "endBoundEntityFace" : qUnion([Q3]), "depth" : 25 * mm});
        }
    });
